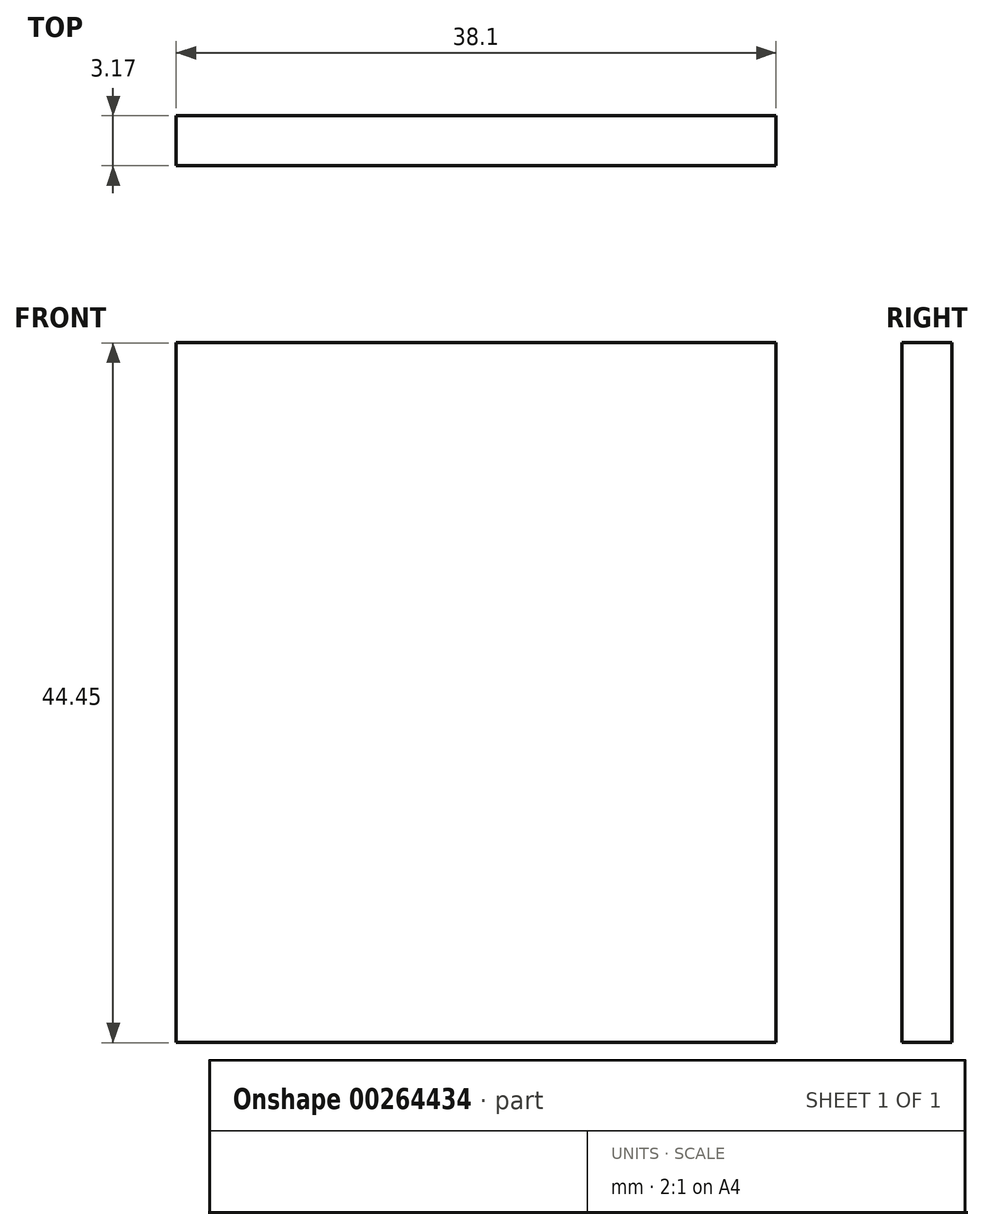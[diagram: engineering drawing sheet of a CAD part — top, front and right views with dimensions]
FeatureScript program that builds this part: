
annotation { "Feature Type Name" : "Feature", "Feature Type Description" : "" }
export const myFeature = defineFeature(function(context is Context, id is Id, definition is map)
    precondition{}
    {
        {
            var Q0;
            Q0=qCreatedBy(makeId("Front.planeOp"),FACE);
            var sketch = newSketch(context, id + "F0", { "sketchPlane" : qUnion([Q0])});
            skLineSegment(sketch, "E0.bottom", {"start": v(19.05, 19.43) * mm, "end": v(-19.05, 19.43) * mm});
            skLineSegment(sketch, "E0.top", {"start": v(19.05, -25.02) * mm, "end": v(-19.05, -25.02) * mm});
            skLineSegment(sketch, "E0.left", {"start": v(19.05, 19.43) * mm, "end": v(19.05, -25.02) * mm});
            skLineSegment(sketch, "E0.right", {"start": v(-19.05, 19.43) * mm, "end": v(-19.05, -25.02) * mm});
            skPoint(sketch, "E0.middle", {"position": v(0, -2.8) * mm});
            skSolve(sketch);
        }
        {
            var Q0;
            Q0 = qSketchRegion(id + "F0", true);
            extrude(context, id + "F1", {"entities" : qUnion([Q0]), "depth" : 3.17 * mm, "offsetDistance" : 25.4 * mm});
        }
    });
